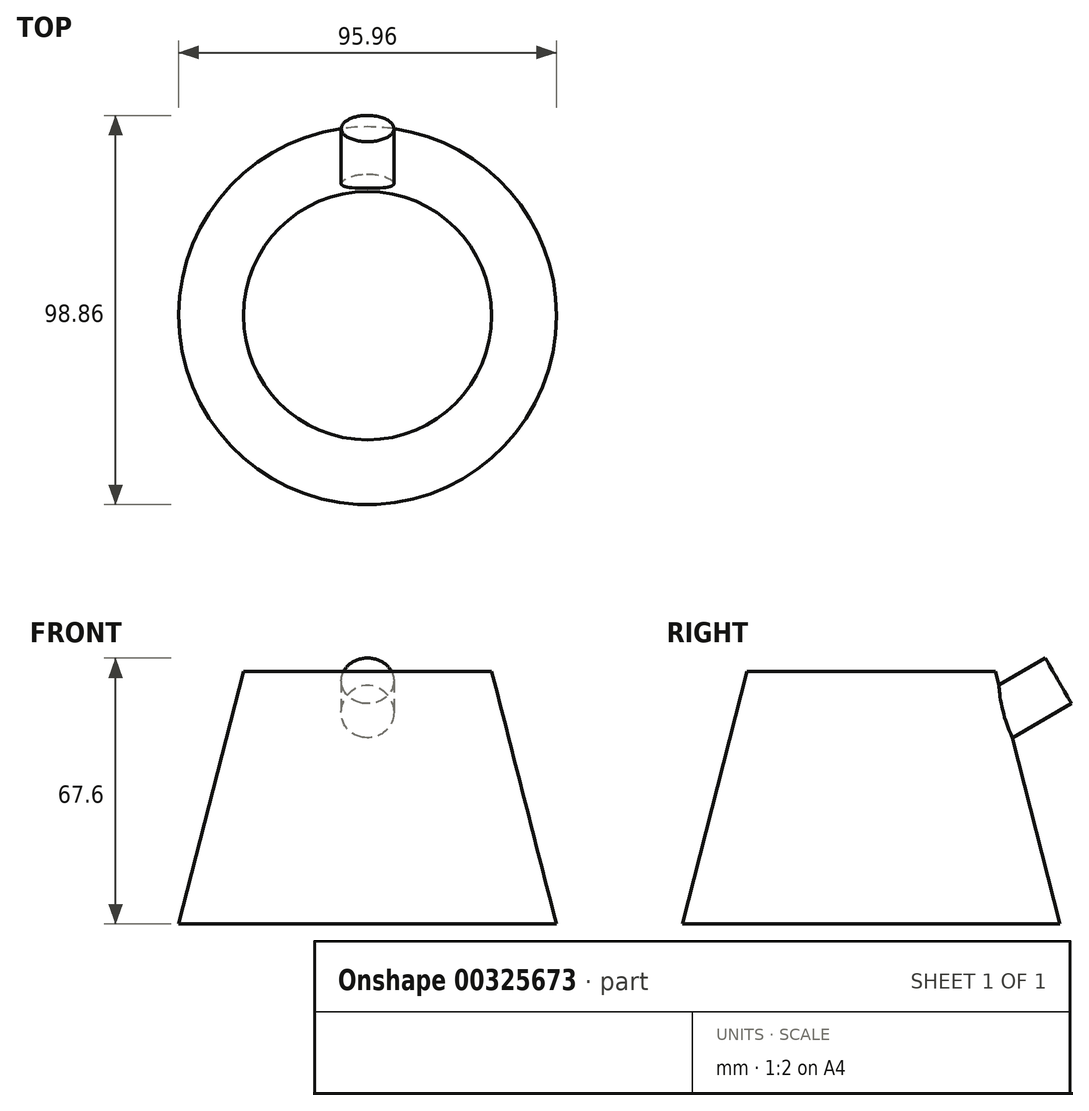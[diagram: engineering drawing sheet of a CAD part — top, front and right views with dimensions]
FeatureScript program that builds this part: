
annotation { "Feature Type Name" : "Feature", "Feature Type Description" : "" }
export const myFeature = defineFeature(function(context is Context, id is Id, definition is map)
    precondition{}
    {
        {
            var Q0;
            Q0=qCreatedBy(makeId("Front.planeOp"),FACE);
            var sketch = newSketch(context, id + "F0", { "sketchPlane" : qUnion([Q0])});
            skLineSegment(sketch, "E0", {"start": v(0, 0) * mm, "end": v(47.98, 0) * mm});
            skLineSegment(sketch, "E1", {"start": v(47.98, 0) * mm, "end": v(31.55, 64.15) * mm});
            skLineSegment(sketch, "E2", {"start": v(31.55, 64.15) * mm, "end": v(0, 64.15) * mm});
            skLineSegment(sketch, "E3", {"start": v(0, 64.15) * mm, "end": v(0, 0) * mm});
            skSolve(sketch);
        }
        {
            var Q0;
            Q0=makeQuery(id+"F0.imprint","IMPRINT",FACE,{"disambiguationData":[TD([[makeQuery(id+"F0.imprint","IMPRINT",EDGE,{"derivedFrom":sQuery(id+"F0.wireOp",EDGE,"E0")}),1.0]])]});
            var Q1;
            Q1=sQuery(id+"F0.wireOp",EDGE,"E3");
            revolve(context, id + "F1", {"entities" : qUnion([Q0]), "axis" : qUnion([Q1]), "revolveType" : RevolveType.ONE_DIRECTION, "angle" : 180 * degree});
        }
        {
            var Q0;
            Q0=makeQuery(id+"F1.opRevolve","CAP_EDGE",EDGE,{"disambiguationData":[OSD([sQuery(id+"F0.wireOp",EDGE,"E2")])],"isStart":true});
            cPlane(context, id + "F2", {"entities" : qUnion([Q0]), "cplaneType" : CPlaneType.LINE_ANGLE, "offset" : 25 * mm, "angle" : 30 * degree, "width" : 150 * mm, "height" : 150 * mm});
        }
        {
            var Q0;
            Q0=makeQuery(id+"F1.opRevolve","SWEPT_BODY",BODY,{"disambiguationData":[OSD([sQuery(id+"F0.wireOp",EDGE,"E0"),sQuery(id+"F0.wireOp",EDGE,"E1"),sQuery(id+"F0.wireOp",EDGE,"E2"),sQuery(id+"F0.wireOp",EDGE,"E3")])]});
            var Q1;
            Q1=qCreatedBy(makeId("Front.planeOp"),FACE);
            mirror(context, id + "F3", {"operationType" : NewBodyOperationType.ADD, "entities" : qUnion([Q0]), "mirrorPlane" : qUnion([Q1])});
        }
        {
            var Q0;
            Q0=qCreatedBy(id+"F2.planeOp",FACE);
            var sketch = newSketch(context, id + "F4", { "sketchPlane" : qUnion([Q0])});
            skCircle(sketch, "E4", {"center": v(0, 29.76) * mm, "radius": 6.68 * mm});
            skSolve(sketch);
        }
        {
            var Q0;
            Q0 = qSketchRegion(id + "F4", true);
            extrude(context, id + "F5", {"entities" : qUnion([Q0]), "operationType" : NewBodyOperationType.ADD, "depth" : 40 * mm});
        }
    });
